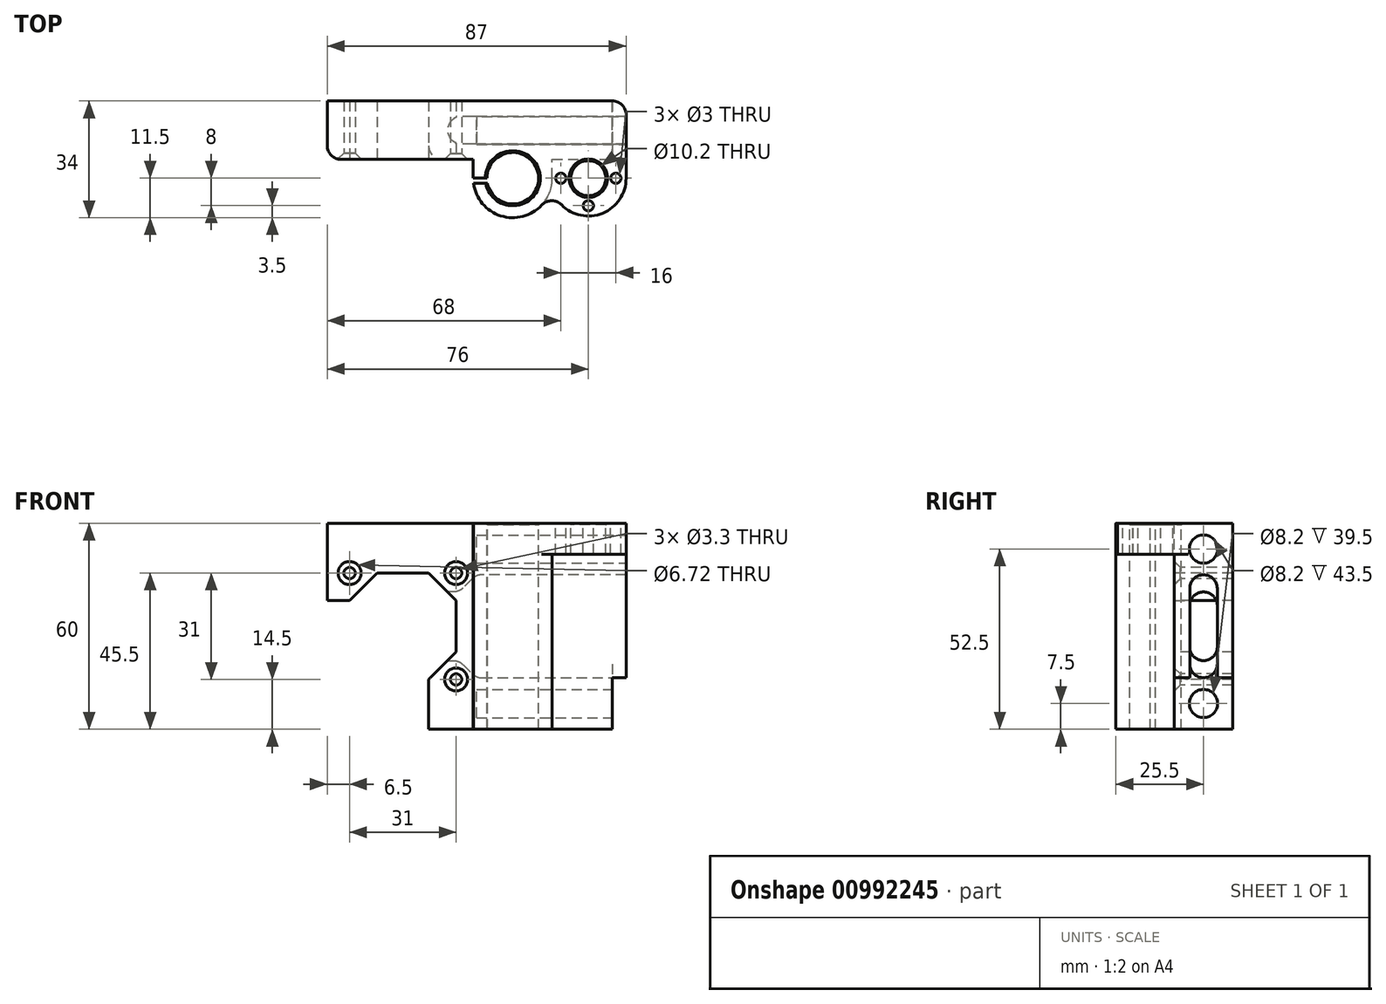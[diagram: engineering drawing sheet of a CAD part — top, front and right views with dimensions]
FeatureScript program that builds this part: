
annotation { "Feature Type Name" : "Feature", "Feature Type Description" : "" }
export const myFeature = defineFeature(function(context is Context, id is Id, definition is map)
    precondition{}
    {
        {
            var Q0;
            Q0=qCreatedBy(makeId("Top.planeOp"),FACE);
            var sketch = newSketch(context, id + "F0", { "sketchPlane" : qUnion([Q0])});
            skArc(sketch, "E0", {"start": v(-7.35, -1.5) * mm, "mid": v(7.46, 0.75) * mm, "end": v(-7.5, 0) * mm});
            skArc(sketch, "E1.0", {"start": v(-11.4, -1.5) * mm, "mid": v(0.75, -11.48) * mm, "end": v(11.5, 0) * mm});
            skCircle(sketch, "E2", {"center": v(22, 0) * mm, "radius": 5.1 * mm});
            skArc(sketch, "E3", {"start": v(14.19, -7.74) * mm, "mid": v(26.19, -10.17) * mm, "end": v(33, 0) * mm});
            skLineSegment(sketch, "E4", {"start": v(-61.05, 14) * mm, "end": v(37.89, 14) * mm, "construction": true});
            skCircle(sketch, "E5", {"center": v(22, 0) * mm, "radius": 8 * mm, "construction": true});
            skLineSegment(sketch, "E6", {"start": v(33, 0) * mm, "end": v(33, 22.5) * mm});
            skLineSegment(sketch, "E7", {"start": v(33, 22.5) * mm, "end": v(-54, 22.5) * mm});
            skLineSegment(sketch, "E8", {"start": v(-54, 22.5) * mm, "end": v(-54, 5.5) * mm});
            skLineSegment(sketch, "E9", {"start": v(-54, 5.5) * mm, "end": v(-11.5, 5.5) * mm});
            skLineSegment(sketch, "E10", {"start": v(-11.5, 5.5) * mm, "end": v(-11.5, 0) * mm});
            skArc(sketch, "E11", {"start": v(14.19, -7.74) * mm, "mid": v(11.28, -6.56) * mm, "end": v(8.42, -7.83) * mm});
            skLineSegment(sketch, "E12", {"start": v(11.5, 0) * mm, "end": v(11.5, 5.5) * mm});
            skLineSegment(sketch, "E13", {"start": v(11.5, 5.5) * mm, "end": v(33, 5.5) * mm});
            skCircle(sketch, "E14", {"center": v(14, 0) * mm, "radius": 1.5 * mm});
            skCircle(sketch, "E15.1.0", {"center": v(22, -8) * mm, "radius": 1.5 * mm});
            skCircle(sketch, "E15.2.0", {"center": v(30, 0) * mm, "radius": 1.5 * mm});
            skLineSegment(sketch, "E15.anchor1", {"start": v(22, 0) * mm, "end": v(14, 0) * mm, "construction": true});
            skLineSegment(sketch, "E15.anchor2", {"start": v(22, 0) * mm, "end": v(30, 0) * mm, "construction": true});
            skLineSegment(sketch, "E16", {"start": v(-7.5, 0) * mm, "end": v(-11.5, 0) * mm});
            skLineSegment(sketch, "E17", {"start": v(-7.35, -1.5) * mm, "end": v(-11.5, -1.5) * mm});
            skSolve(sketch);
        }
        {
            var Q0;
            Q0=makeQuery(id+"F0.imprint","IMPRINT",FACE,{"disambiguationData":[TD([[makeQuery(id+"F0.imprint","IMPRINT",EDGE,{"derivedFrom":sQuery(id+"F0.wireOp",EDGE,"E0")}),-1.0]])]});
            extrude(context, id + "F1", {"entities" : qUnion([Q0]), "oppositeDirection" : true, "depth" : 60 * mm, "offsetDistance" : 25 * mm});
        }
        {
            var Q0;
            Q0=qSketchRegion(id+"F0",true);
            extrude(context, id + "F2", {"entities" : qUnion([Q0]), "operationType" : NewBodyOperationType.ADD, "oppositeDirection" : true, "depth" : 9 * mm, "offsetDistance" : 25 * mm});
        }
        {
            var Q0;
            Q0=makeQuery(id+"F1.opExtrude","SWEPT_EDGE",EDGE,{"disambiguationData":[OSD([sQuery(id+"F0.wireOp",EDGE,"E8"),sQuery(id+"F0.wireOp",EDGE,"E9")])]});
            var Q1;
            Q1=makeQuery(id+"F1.opExtrude","SWEPT_EDGE",EDGE,{"disambiguationData":[OSD([sQuery(id+"F0.wireOp",EDGE,"E6"),sQuery(id+"F0.wireOp",EDGE,"E13")])]});
            var Q2;
            Q2=makeQuery(id+"F1.opExtrude","SWEPT_EDGE",EDGE,{"disambiguationData":[OSD([sQuery(id+"F0.wireOp",EDGE,"E6"),sQuery(id+"F0.wireOp",EDGE,"E7")])]});
            fillet(context, id + "F3", {"entities" : qUnion([Q0, Q1, Q2]), "radius" : 4 * mm, "tangentPropagation" : true, "allowEdgeOverflow" : false});
        }
        {
            var Q0;
            Q0=qCreatedBy(makeId("Front.planeOp"),FACE);
            var sketch = newSketch(context, id + "F4", { "sketchPlane" : qUnion([Q0])});
            skCircle(sketch, "E18", {"center": v(-32, -30) * mm, "radius": 15.5 * mm, "construction": true});
            skLineSegment(sketch, "E19", {"start": v(-57.77, -22.5) * mm, "end": v(-47.5, -22.5) * mm});
            skLineSegment(sketch, "E20", {"start": v(-47.5, -22.5) * mm, "end": v(-39.5, -14.5) * mm});
            skLineSegment(sketch, "E21", {"start": v(-39.5, -14.5) * mm, "end": v(-24.5, -14.5) * mm});
            skLineSegment(sketch, "E22", {"start": v(-24.5, -14.5) * mm, "end": v(-16.5, -22.5) * mm});
            skLineSegment(sketch, "E23", {"start": v(-16.5, -22.5) * mm, "end": v(-16.5, -37.5) * mm});
            skLineSegment(sketch, "E24", {"start": v(-16.5, -37.5) * mm, "end": v(-24.5, -45.5) * mm});
            skLineSegment(sketch, "E25", {"start": v(-24.5, -45.5) * mm, "end": v(-24.5, -64.37) * mm});
            skLineSegment(sketch, "E26", {"start": v(-24.5, -64.37) * mm, "end": v(-57.77, -64.37) * mm});
            skLineSegment(sketch, "E27", {"start": v(-57.77, -64.37) * mm, "end": v(-57.77, -22.5) * mm});
            skLineSegment(sketch, "E28.bottom", {"start": v(36.46, -61.87) * mm, "end": v(29, -61.87) * mm});
            skLineSegment(sketch, "E28.top", {"start": v(36.46, -45) * mm, "end": v(29, -45) * mm});
            skLineSegment(sketch, "E28.left", {"start": v(36.46, -61.87) * mm, "end": v(36.46, -45) * mm});
            skLineSegment(sketch, "E28.right", {"start": v(29, -61.87) * mm, "end": v(29, -45) * mm});
            skSolve(sketch);
        }
        {
            var Q0;
            Q0=qSketchRegion(id+"F4",true);
            extrude(context, id + "F5", {"entities" : qUnion([Q0]), "operationType" : NewBodyOperationType.REMOVE, "endBound" : BoundingType.THROUGH_ALL, "oppositeDirection" : true, "depth" : 25 * mm, "offsetDistance" : 25 * mm});
        }
        {
            var Q0;
            {var subQ0=sQuery(id+"F0.wireOp",EDGE,"E6");Q0=makeQuery(id+"F2.boolean.opBoolean","MERGE",FACE,{"derivedFrom":[makeQuery(id+"F1.opExtrude","SWEPT_FACE",FACE,{"disambiguationData":[OSD([subQ0])]}),makeQuery(id+"F2.opExtrude","SWEPT_FACE",FACE,{"disambiguationData":[OSD([subQ0])]})]});}
            var sketch = newSketch(context, id + "F6", { "sketchPlane" : qUnion([Q0])});
            skCircle(sketch, "E29", {"center": v(14, -7.5) * mm, "radius": 4.1 * mm});
            skCircle(sketch, "E30", {"center": v(14, -52.5) * mm, "radius": 4.1 * mm});
            skSolve(sketch);
        }
        {
            var Q0;
            Q0=qSketchRegion(id+"F6",true);
            extrude(context, id + "F7", {"entities" : qUnion([Q0]), "operationType" : NewBodyOperationType.REMOVE, "oppositeDirection" : true, "depth" : 43.5 * mm, "offsetDistance" : 25 * mm});
        }
        {
            var Q0;
            Q0=qCreatedBy(makeId("Front.planeOp"),FACE);
            cPlane(context, id + "F8", {"entities" : qUnion([Q0]), "cplaneType" : CPlaneType.OFFSET, "offset" : 14 * mm, "oppositeDirection" : true, "width" : 150 * mm, "height" : 150 * mm});
        }
        {
            var Q0;
            Q0=qCreatedBy(id+"F8.planeOp",FACE);
            var sketch = newSketch(context, id + "F9", { "sketchPlane" : qUnion([Q0])});
            skLineSegment(sketch, "E31", {"start": v(-21.87, -20) * mm, "end": v(-17.31, -20) * mm});
            skLineSegment(sketch, "E32", {"start": v(-14.49, -18.83) * mm, "end": v(-11.83, -16.17) * mm});
            skLineSegment(sketch, "E33", {"start": v(-9, -15) * mm, "end": v(34.4, -15) * mm});
            skLineSegment(sketch, "E34", {"start": v(34.4, -15) * mm, "end": v(34.4, -45) * mm});
            skLineSegment(sketch, "E35", {"start": v(34.4, -45) * mm, "end": v(-9, -45) * mm});
            skLineSegment(sketch, "E36", {"start": v(-11.83, -43.83) * mm, "end": v(-14.49, -41.17) * mm});
            skLineSegment(sketch, "E37", {"start": v(-17.31, -40) * mm, "end": v(-21.87, -40) * mm});
            skLineSegment(sketch, "E38", {"start": v(-21.87, -40) * mm, "end": v(-21.87, -20) * mm});
            skPoint(sketch, "E39.visualSharp", {"position": v(-10.66, -45) * mm});
            skArc(sketch, "E39.filletArc", {"start": v(-11.83, -43.83) * mm, "mid": v(-10.53, -44.7) * mm, "end": v(-9, -45) * mm});
            skPoint(sketch, "E40.visualSharp", {"position": v(-15.66, -40) * mm});
            skArc(sketch, "E40.filletArc", {"start": v(-14.49, -41.17) * mm, "mid": v(-15.78, -40.3) * mm, "end": v(-17.31, -40) * mm});
            skPoint(sketch, "E41.visualSharp", {"position": v(-10.66, -15) * mm});
            skArc(sketch, "E41.filletArc", {"start": v(-9, -15) * mm, "mid": v(-10.53, -15.3) * mm, "end": v(-11.83, -16.17) * mm});
            skPoint(sketch, "E42.visualSharp", {"position": v(-15.66, -20) * mm});
            skArc(sketch, "E42.filletArc", {"start": v(-17.31, -20) * mm, "mid": v(-15.78, -19.7) * mm, "end": v(-14.49, -18.83) * mm});
            skSolve(sketch);
        }
        {
            var Q0;
            Q0=makeQuery(id+"F1.opExtrude","SWEPT_FACE",FACE,{"disambiguationData":[OSD([sQuery(id+"F0.wireOp",EDGE,"E9")])]});
            var sketch = newSketch(context, id + "F10", { "sketchPlane" : qUnion([Q0])});
            skPoint(sketch, "E43", {"position": v(-47.5, -14.5) * mm});
            skPoint(sketch, "E44", {"position": v(-16.5, -14.5) * mm});
            skPoint(sketch, "E45", {"position": v(-16.5, -45.5) * mm});
            skSolve(sketch);
        }
        {
            var Q0;
            Q0=sQuery(id+"F10.wireOp",VERTEX,"E43");
            var Q1;
            Q1=sQuery(id+"F10.wireOp",VERTEX,"E45");
            var Q2;
            Q2=sQuery(id+"F10.wireOp",VERTEX,"E44");
            var Q3;
            Q3=makeQuery(id+"F1.opExtrude","SWEPT_BODY",BODY,{"disambiguationData":[OSD([sQuery(id+"F0.wireOp",EDGE,"E0"),sQuery(id+"F0.wireOp",EDGE,"E1.0"),sQuery(id+"F0.wireOp",EDGE,"E6"),sQuery(id+"F0.wireOp",EDGE,"E7"),sQuery(id+"F0.wireOp",EDGE,"E8"),sQuery(id+"F0.wireOp",EDGE,"E9"),sQuery(id+"F0.wireOp",EDGE,"E10"),sQuery(id+"F0.wireOp",EDGE,"E12"),sQuery(id+"F0.wireOp",EDGE,"E13")])]});
            hole(context, id + "F11", {"style" : HoleStyle.C_SINK, "endStyle" : HoleEndStyle.BLIND, "standardTappedOrClearance" : lookupTablePath({ "fit" : "Normal", "standard" : "ISO", "size" : "M3", "type" : "Clearance" }), "standardBlindInLast" : lookupTablePath({ "fit" : "Standard", "standard" : "ISO", "size" : "M3", "type" : "Clearance" }), "holeDiameter" : 3.3 * mm, "cSinkDiameter" : 6.72 * mm, "cSinkAngle" : 90 * degree, "majorDiameter" : 5 * mm, "holeDepth" : 20 * mm, "isTappedThrough" : true, "tappedDepth" : 12 * mm, "tapClearance" : 3, "locations" : qUnion([Q0, Q1, Q2]), "scope" : qUnion([Q3])});
        }
        {
            var Q0;
            Q0=qSketchRegion(id+"F9",true);
            extrude(context, id + "F12", {"entities" : qUnion([Q0]), "operationType" : NewBodyOperationType.REMOVE, "endBound" : BoundingType.SYMMETRIC, "depth" : 8 * mm, "offsetDistance" : 25 * mm});
        }
        {
            var Q0;
            Q0=makeQuery(id+"F5.boolean.opBoolean","INTERSECT",EDGE,{"derivedFrom":[makeQuery(id+"F1.opExtrude","SWEPT_FACE",FACE,{"disambiguationData":[OSD([sQuery(id+"F0.wireOp",EDGE,"E9")])]}),makeQuery(id+"F5.opExtrude","SWEPT_FACE",FACE,{"disambiguationData":[OSD([sQuery(id+"F4.wireOp",EDGE,"E25")])]})]});
            fillet(context, id + "F13", {"entities" : qUnion([Q0]), "radius" : 4 * mm, "tangentPropagation" : true, "allowEdgeOverflow" : false});
        }
        {
            var Q0;
            Q0=makeQuery(id+"F1.opExtrude","CAP_EDGE",EDGE,{"disambiguationData":[OSD([sQuery(id+"F0.wireOp",EDGE,"E0")])],"isStart":true});
            var Q1;
            Q1=makeQuery(id+"F2.opExtrude","CAP_EDGE",EDGE,{"disambiguationData":[OSD([sQuery(id+"F0.wireOp",EDGE,"E2")])],"isStart":true});
            chamfer(context, id + "F14", {"entities" : qUnion([Q0, Q1]), "chamferType" : ChamferType.TWO_OFFSETS, "width1" : 0.4 * mm, "oppositeDirection" : false, "width2" : 0.5 * mm, "tangentPropagation" : true});
        }
        {
            var Q0;
            Q0=makeQuery(id+"F12.boolean.opBoolean","COPY",EDGE,{"derivedFrom":makeQuery(id+"F12.opExtrude","CAP_EDGE",EDGE,{"disambiguationData":[OSD([sQuery(id+"F9.wireOp",EDGE,"E33")])],"isStart":false})});
            var Q1;
            Q1=makeQuery(id+"F12.boolean.opBoolean","COPY",EDGE,{"derivedFrom":makeQuery(id+"F12.opExtrude","CAP_EDGE",EDGE,{"disambiguationData":[OSD([sQuery(id+"F9.wireOp",EDGE,"E33")])],"isStart":true})});
            var Q2;
            {var subQ0=sQuery(id+"F9.wireOp",EDGE,"E35");Q2=makeQuery(id+"F12.boolean.opBoolean","COPY",EDGE,{"disambiguationData":[topologyDisambiguationEdgeConnected([makeQuery(id+"F12.opExtrude","SWEPT_FACE",FACE,{"disambiguationData":[OSD([subQ0])]})])],"derivedFrom":makeQuery(id+"F12.opExtrude","CAP_EDGE",EDGE,{"disambiguationData":[OSD([subQ0])],"isStart":false})});}
            var Q3;
            {var subQ0=sQuery(id+"F9.wireOp",EDGE,"E35");Q3=makeQuery(id+"F12.boolean.opBoolean","COPY",EDGE,{"disambiguationData":[topologyDisambiguationEdgeConnected([makeQuery(id+"F12.opExtrude","SWEPT_FACE",FACE,{"disambiguationData":[OSD([subQ0])]})])],"derivedFrom":makeQuery(id+"F12.opExtrude","CAP_EDGE",EDGE,{"disambiguationData":[OSD([subQ0])],"isStart":true})});}
            fillet(context, id + "F15", {"entities" : qUnion([Q0, Q1, Q2, Q3]), "radius" : 4 * mm, "tangentPropagation" : true, "allowEdgeOverflow" : false});
        }
    });
